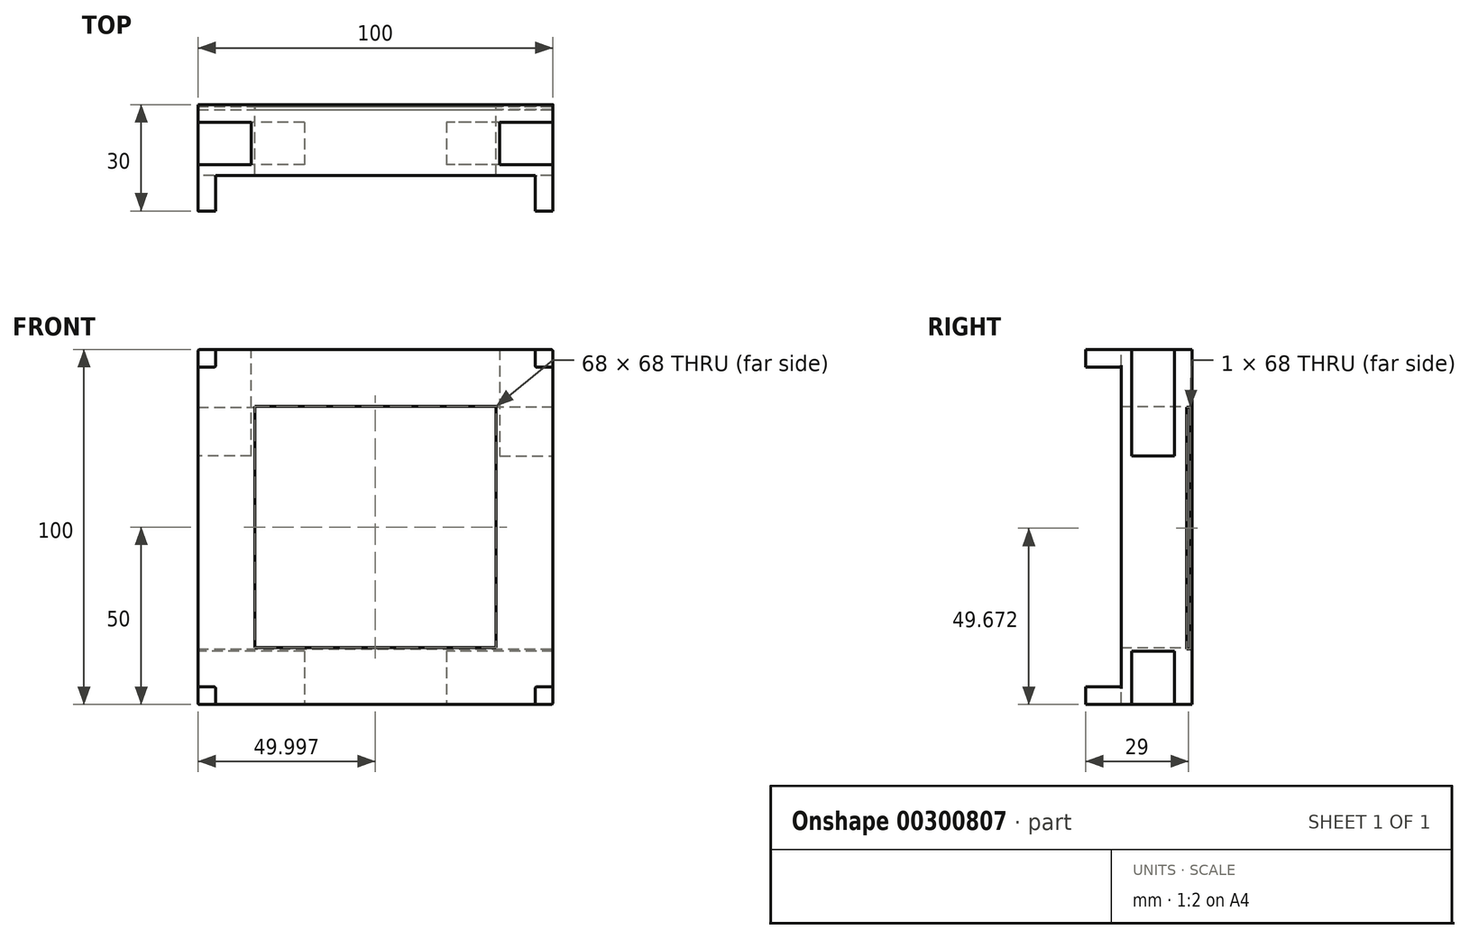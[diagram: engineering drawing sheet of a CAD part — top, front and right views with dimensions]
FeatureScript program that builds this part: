
annotation { "Feature Type Name" : "Feature", "Feature Type Description" : "" }
export const myFeature = defineFeature(function(context is Context, id is Id, definition is map)
    precondition{}
    {
        {
            var Q0;
            Q0=qCreatedBy(makeId("Front.planeOp"),FACE);
            var sketch = newSketch(context, id + "F0", { "sketchPlane" : qUnion([Q0])});
            skLineSegment(sketch, "E0.bottom", {"start": v(-49.23, 948.9) * mm, "end": v(950.77, 948.9) * mm});
            skLineSegment(sketch, "E0.top", {"start": v(-49.23, -51.1) * mm, "end": v(950.77, -51.1) * mm});
            skLineSegment(sketch, "E0.left", {"start": v(-49.23, 948.9) * mm, "end": v(-49.23, -51.1) * mm});
            skLineSegment(sketch, "E0.right", {"start": v(950.77, 948.9) * mm, "end": v(950.77, -51.1) * mm});
            skSolve(sketch);
        }
        {
            var Q0;
            Q0=qSketchRegion(id+"F0",true);
            extrude(context, id + "F1", {"entities" : qUnion([Q0]), "depth" : 300 * mm});
        }
        {
            var Q0;
            Q0=makeQuery(id+"F1.opExtrude","SWEPT_FACE",FACE,{"disambiguationData":[OSD([sQuery(id+"F0.wireOp",EDGE,"E0.bottom")])]});
            var sketch = newSketch(context, id + "F2", { "sketchPlane" : qUnion([Q0])});
            skLineSegment(sketch, "E1.bottom", {"start": v(0.77, -300) * mm, "end": v(900.77, -300) * mm});
            skLineSegment(sketch, "E1.top", {"start": v(0.77, -200) * mm, "end": v(900.77, -200) * mm});
            skLineSegment(sketch, "E1.left", {"start": v(0.77, -300) * mm, "end": v(0.77, -200) * mm});
            skLineSegment(sketch, "E1.right", {"start": v(900.77, -300) * mm, "end": v(900.77, -200) * mm});
            skSolve(sketch);
        }
        {
            var Q0;
            Q0=qSketchRegion(id+"F2",true);
            extrude(context, id + "F3", {"entities" : qUnion([Q0]), "operationType" : NewBodyOperationType.REMOVE, "endBound" : BoundingType.THROUGH_ALL, "oppositeDirection" : true, "depth" : 100 * mm});
        }
        {
            var Q0;
            Q0=makeQuery(id+"F1.opExtrude","SWEPT_FACE",FACE,{"disambiguationData":[OSD([sQuery(id+"F0.wireOp",EDGE,"E0.left")])]});
            var sketch = newSketch(context, id + "F4", { "sketchPlane" : qUnion([Q0])});
            skLineSegment(sketch, "E2.bottom", {"start": v(300, -1.1) * mm, "end": v(200, -1.1) * mm});
            skLineSegment(sketch, "E2.top", {"start": v(300, 898.9) * mm, "end": v(200, 898.9) * mm});
            skLineSegment(sketch, "E2.left", {"start": v(300, -1.1) * mm, "end": v(300, 898.9) * mm});
            skLineSegment(sketch, "E2.right", {"start": v(200, -1.1) * mm, "end": v(200, 898.9) * mm});
            skSolve(sketch);
        }
        {
            var Q0;
            Q0=qSketchRegion(id+"F4",true);
            extrude(context, id + "F5", {"entities" : qUnion([Q0]), "operationType" : NewBodyOperationType.REMOVE, "endBound" : BoundingType.THROUGH_ALL, "oppositeDirection" : true, "depth" : 25 * mm});
        }
        {
            var Q0;
            Q0=makeQuery(id+"F1.opExtrude","SWEPT_FACE",FACE,{"disambiguationData":[OSD([sQuery(id+"F0.wireOp",EDGE,"E0.top")])]});
            var sketch = newSketch(context, id + "F6", { "sketchPlane" : qUnion([Q0])});
            skLineSegment(sketch, "E3.bottom", {"start": v(250.77, 50) * mm, "end": v(-49.23, 50) * mm});
            skLineSegment(sketch, "E3.top", {"start": v(250.77, 170) * mm, "end": v(-49.23, 170) * mm});
            skLineSegment(sketch, "E3.left", {"start": v(250.77, 50) * mm, "end": v(250.77, 170) * mm});
            skLineSegment(sketch, "E3.right", {"start": v(-49.23, 50) * mm, "end": v(-49.23, 170) * mm});
            skSolve(sketch);
        }
        {
            var Q0;
            Q0=qSketchRegion(id+"F6",true);
            extrude(context, id + "F7", {"entities" : qUnion([Q0]), "operationType" : NewBodyOperationType.REMOVE, "oppositeDirection" : true, "depth" : 150 * mm});
        }
        {
            var Q0;
            Q0=makeQuery(id+"F1.opExtrude","SWEPT_FACE",FACE,{"disambiguationData":[OSD([sQuery(id+"F0.wireOp",EDGE,"E0.top")])]});
            var sketch = newSketch(context, id + "F8", { "sketchPlane" : qUnion([Q0])});
            skLineSegment(sketch, "E4.bottom", {"start": v(950.77, 50) * mm, "end": v(650.77, 50) * mm});
            skLineSegment(sketch, "E4.top", {"start": v(950.77, 170) * mm, "end": v(650.77, 170) * mm});
            skLineSegment(sketch, "E4.left", {"start": v(950.77, 50) * mm, "end": v(950.77, 170) * mm});
            skLineSegment(sketch, "E4.right", {"start": v(650.77, 50) * mm, "end": v(650.77, 170) * mm});
            skSolve(sketch);
        }
        {
            var Q0;
            Q0=qSketchRegion(id+"F8",true);
            extrude(context, id + "F9", {"entities" : qUnion([Q0]), "operationType" : NewBodyOperationType.REMOVE, "oppositeDirection" : true, "depth" : 150 * mm});
        }
        {
            var Q0;
            Q0=makeQuery(id+"F1.opExtrude","SWEPT_FACE",FACE,{"disambiguationData":[OSD([sQuery(id+"F0.wireOp",EDGE,"E0.right")])]});
            var sketch = newSketch(context, id + "F10", { "sketchPlane" : qUnion([Q0])});
            skLineSegment(sketch, "E5.bottom", {"start": v(-50, 948.9) * mm, "end": v(-170, 948.9) * mm});
            skLineSegment(sketch, "E5.top", {"start": v(-50, 648.9) * mm, "end": v(-170, 648.9) * mm});
            skLineSegment(sketch, "E5.left", {"start": v(-50, 948.9) * mm, "end": v(-50, 648.9) * mm});
            skLineSegment(sketch, "E5.right", {"start": v(-170, 948.9) * mm, "end": v(-170, 648.9) * mm});
            skSolve(sketch);
        }
        {
            var Q0;
            Q0=qSketchRegion(id+"F10",true);
            extrude(context, id + "F11", {"entities" : qUnion([Q0]), "operationType" : NewBodyOperationType.REMOVE, "oppositeDirection" : true, "depth" : 150 * mm});
        }
        {
            var Q0;
            Q0=makeQuery(id+"F1.opExtrude","SWEPT_FACE",FACE,{"disambiguationData":[OSD([sQuery(id+"F0.wireOp",EDGE,"E0.left")])]});
            var sketch = newSketch(context, id + "F12", { "sketchPlane" : qUnion([Q0])});
            skLineSegment(sketch, "E6.bottom", {"start": v(50, 648.9) * mm, "end": v(170, 648.9) * mm});
            skLineSegment(sketch, "E6.top", {"start": v(50, 948.9) * mm, "end": v(170, 948.9) * mm});
            skLineSegment(sketch, "E6.left", {"start": v(50, 648.9) * mm, "end": v(50, 948.9) * mm});
            skLineSegment(sketch, "E6.right", {"start": v(170, 648.9) * mm, "end": v(170, 948.9) * mm});
            skSolve(sketch);
        }
        {
            var Q0;
            Q0=qSketchRegion(id+"F12",true);
            extrude(context, id + "F13", {"entities" : qUnion([Q0]), "operationType" : NewBodyOperationType.REMOVE, "oppositeDirection" : true, "depth" : 150 * mm});
        }
        {
            var Q0;
            {var subQ0=sQuery(id+"F0.wireOp",EDGE,"E0.right");var subQ1=sQuery(id+"F0.wireOp",EDGE,"E0.top");Q0=makeQuery(id+"F9.boolean.opBoolean","SPLIT",EDGE,{"disambiguationData":[TD([makeQuery(id+"F9.opExtrude","SWEPT_FACE",FACE,{"disambiguationData":[OSD([sQuery(id+"F8.wireOp",EDGE,"E4.top")])]})])],"derivedFrom":makeQuery(id+"F1.opExtrude","SWEPT_EDGE",EDGE,{"disambiguationData":[OSD([subQ1,subQ0])]})});}
            var Q1;
            Q1=makeQuery(id+"F3.boolean.opBoolean","INTERSECT",EDGE,{"derivedFrom":[makeQuery(id+"F1.opExtrude","SWEPT_FACE",FACE,{"disambiguationData":[OSD([sQuery(id+"F0.wireOp",EDGE,"E0.top")])]}),makeQuery(id+"F3.opExtrude","SWEPT_FACE",FACE,{"disambiguationData":[OSD([sQuery(id+"F2.wireOp",EDGE,"E1.right")])]})]});
            var Q2;
            Q2=makeQuery(id+"F5.boolean.opBoolean","INTERSECT",EDGE,{"derivedFrom":[makeQuery(id+"F1.opExtrude","SWEPT_FACE",FACE,{"disambiguationData":[OSD([sQuery(id+"F0.wireOp",EDGE,"E0.right")])]}),makeQuery(id+"F5.opExtrude","SWEPT_FACE",FACE,{"disambiguationData":[OSD([sQuery(id+"F4.wireOp",EDGE,"E2.bottom")])]})]});
            var Q3;
            Q3=makeQuery(id+"F5.boolean.opBoolean","INTERSECT",EDGE,{"derivedFrom":[makeQuery(id+"F3.boolean.opBoolean","COPY",FACE,{"derivedFrom":makeQuery(id+"F3.opExtrude","SWEPT_FACE",FACE,{"disambiguationData":[OSD([sQuery(id+"F2.wireOp",EDGE,"E1.right")])]})}),makeQuery(id+"F5.opExtrude","SWEPT_FACE",FACE,{"disambiguationData":[OSD([sQuery(id+"F4.wireOp",EDGE,"E2.bottom")])]})]});
            var Q4;
            {var subQ0=sQuery(id+"F0.wireOp",EDGE,"E0.left");var subQ1=sQuery(id+"F0.wireOp",EDGE,"E0.top");Q4=makeQuery(id+"F7.boolean.opBoolean","SPLIT",EDGE,{"disambiguationData":[TD([makeQuery(id+"F7.opExtrude","SWEPT_FACE",FACE,{"disambiguationData":[OSD([sQuery(id+"F6.wireOp",EDGE,"E3.top")])]})])],"derivedFrom":makeQuery(id+"F1.opExtrude","SWEPT_EDGE",EDGE,{"disambiguationData":[OSD([subQ1,subQ0])]})});}
            var Q5;
            Q5=makeQuery(id+"F3.boolean.opBoolean","INTERSECT",EDGE,{"derivedFrom":[makeQuery(id+"F1.opExtrude","SWEPT_FACE",FACE,{"disambiguationData":[OSD([sQuery(id+"F0.wireOp",EDGE,"E0.top")])]}),makeQuery(id+"F3.opExtrude","SWEPT_FACE",FACE,{"disambiguationData":[OSD([sQuery(id+"F2.wireOp",EDGE,"E1.left")])]})]});
            var Q6;
            Q6=makeQuery(id+"F5.boolean.opBoolean","COPY",EDGE,{"derivedFrom":makeQuery(id+"F5.opExtrude","CAP_EDGE",EDGE,{"disambiguationData":[OSD([sQuery(id+"F4.wireOp",EDGE,"E2.bottom")])],"isStart":true})});
            var Q7;
            Q7=makeQuery(id+"F5.boolean.opBoolean","INTERSECT",EDGE,{"derivedFrom":[makeQuery(id+"F3.boolean.opBoolean","COPY",FACE,{"derivedFrom":makeQuery(id+"F3.opExtrude","SWEPT_FACE",FACE,{"disambiguationData":[OSD([sQuery(id+"F2.wireOp",EDGE,"E1.left")])]})}),makeQuery(id+"F5.opExtrude","SWEPT_FACE",FACE,{"disambiguationData":[OSD([sQuery(id+"F4.wireOp",EDGE,"E2.bottom")])]})]});
            var Q8;
            {var subQ0=sQuery(id+"F0.wireOp",EDGE,"E0.bottom");var subQ1=sQuery(id+"F0.wireOp",EDGE,"E0.left");Q8=makeQuery(id+"F13.boolean.opBoolean","SPLIT",EDGE,{"disambiguationData":[TD([makeQuery(id+"F13.opExtrude","SWEPT_FACE",FACE,{"disambiguationData":[OSD([sQuery(id+"F12.wireOp",EDGE,"E6.right")])]})])],"derivedFrom":makeQuery(id+"F1.opExtrude","SWEPT_EDGE",EDGE,{"disambiguationData":[OSD([subQ0,subQ1])]})});}
            var Q9;
            Q9=makeQuery(id+"F3.boolean.opBoolean","COPY",EDGE,{"derivedFrom":makeQuery(id+"F3.opExtrude","CAP_EDGE",EDGE,{"disambiguationData":[OSD([sQuery(id+"F2.wireOp",EDGE,"E1.left")])],"isStart":true})});
            var Q10;
            Q10=makeQuery(id+"F5.boolean.opBoolean","COPY",EDGE,{"derivedFrom":makeQuery(id+"F5.opExtrude","CAP_EDGE",EDGE,{"disambiguationData":[OSD([sQuery(id+"F4.wireOp",EDGE,"E2.top")])],"isStart":true})});
            var Q11;
            Q11=makeQuery(id+"F5.boolean.opBoolean","INTERSECT",EDGE,{"derivedFrom":[makeQuery(id+"F3.boolean.opBoolean","COPY",FACE,{"derivedFrom":makeQuery(id+"F3.opExtrude","SWEPT_FACE",FACE,{"disambiguationData":[OSD([sQuery(id+"F2.wireOp",EDGE,"E1.left")])]})}),makeQuery(id+"F5.opExtrude","SWEPT_FACE",FACE,{"disambiguationData":[OSD([sQuery(id+"F4.wireOp",EDGE,"E2.top")])]})]});
            var Q12;
            {var subQ0=sQuery(id+"F0.wireOp",EDGE,"E0.bottom");var subQ1=sQuery(id+"F0.wireOp",EDGE,"E0.right");Q12=makeQuery(id+"F11.boolean.opBoolean","SPLIT",EDGE,{"disambiguationData":[TD([makeQuery(id+"F11.opExtrude","SWEPT_FACE",FACE,{"disambiguationData":[OSD([sQuery(id+"F10.wireOp",EDGE,"E5.right")])]})])],"derivedFrom":makeQuery(id+"F1.opExtrude","SWEPT_EDGE",EDGE,{"disambiguationData":[OSD([subQ0,subQ1])]})});}
            var Q13;
            Q13=makeQuery(id+"F5.boolean.opBoolean","INTERSECT",EDGE,{"derivedFrom":[makeQuery(id+"F1.opExtrude","SWEPT_FACE",FACE,{"disambiguationData":[OSD([sQuery(id+"F0.wireOp",EDGE,"E0.right")])]}),makeQuery(id+"F5.opExtrude","SWEPT_FACE",FACE,{"disambiguationData":[OSD([sQuery(id+"F4.wireOp",EDGE,"E2.top")])]})]});
            var Q14;
            Q14=makeQuery(id+"F5.boolean.opBoolean","INTERSECT",EDGE,{"derivedFrom":[makeQuery(id+"F3.boolean.opBoolean","COPY",FACE,{"derivedFrom":makeQuery(id+"F3.opExtrude","SWEPT_FACE",FACE,{"disambiguationData":[OSD([sQuery(id+"F2.wireOp",EDGE,"E1.right")])]})}),makeQuery(id+"F5.opExtrude","SWEPT_FACE",FACE,{"disambiguationData":[OSD([sQuery(id+"F4.wireOp",EDGE,"E2.top")])]})]});
            var Q15;
            Q15=makeQuery(id+"F3.boolean.opBoolean","COPY",EDGE,{"derivedFrom":makeQuery(id+"F3.opExtrude","CAP_EDGE",EDGE,{"disambiguationData":[OSD([sQuery(id+"F2.wireOp",EDGE,"E1.right")])],"isStart":true})});
            fillet(context, id + "F14", {"entities" : qUnion([Q0, Q1, Q2, Q3, Q4, Q5, Q6, Q7, Q8, Q9, Q10, Q11, Q12, Q13, Q14, Q15]), "radius" : 5 * mm, "tangentPropagation" : true, "allowEdgeOverflow" : false});
        }
        {
            var Q0;
            {var subQ0=sQuery(id+"F0.wireOp",EDGE,"E0.bottom");var subQ1=sQuery(id+"F0.wireOp",EDGE,"E0.right");Q0=makeQuery(id+"F11.boolean.opBoolean","SPLIT",EDGE,{"disambiguationData":[TD([makeQuery(id+"F11.opExtrude","SWEPT_FACE",FACE,{"disambiguationData":[OSD([sQuery(id+"F10.wireOp",EDGE,"E5.left")])]})])],"derivedFrom":makeQuery(id+"F1.opExtrude","SWEPT_EDGE",EDGE,{"disambiguationData":[OSD([subQ0,subQ1])]})});}
            var Q1;
            {var subQ0=sQuery(id+"F0.wireOp",EDGE,"E0.right");var subQ1=sQuery(id+"F0.wireOp",EDGE,"E0.top");Q1=makeQuery(id+"F9.boolean.opBoolean","SPLIT",EDGE,{"disambiguationData":[TD([makeQuery(id+"F9.opExtrude","SWEPT_FACE",FACE,{"disambiguationData":[OSD([sQuery(id+"F8.wireOp",EDGE,"E4.bottom")])]})])],"derivedFrom":makeQuery(id+"F1.opExtrude","SWEPT_EDGE",EDGE,{"disambiguationData":[OSD([subQ1,subQ0])]})});}
            var Q2;
            {var subQ0=sQuery(id+"F0.wireOp",EDGE,"E0.left");var subQ1=sQuery(id+"F0.wireOp",EDGE,"E0.top");Q2=makeQuery(id+"F7.boolean.opBoolean","SPLIT",EDGE,{"disambiguationData":[TD([makeQuery(id+"F7.opExtrude","SWEPT_FACE",FACE,{"disambiguationData":[OSD([sQuery(id+"F6.wireOp",EDGE,"E3.bottom")])]})])],"derivedFrom":makeQuery(id+"F1.opExtrude","SWEPT_EDGE",EDGE,{"disambiguationData":[OSD([subQ1,subQ0])]})});}
            var Q3;
            {var subQ0=sQuery(id+"F0.wireOp",EDGE,"E0.bottom");var subQ1=sQuery(id+"F0.wireOp",EDGE,"E0.left");Q3=makeQuery(id+"F13.boolean.opBoolean","SPLIT",EDGE,{"disambiguationData":[TD([makeQuery(id+"F13.opExtrude","SWEPT_FACE",FACE,{"disambiguationData":[OSD([sQuery(id+"F12.wireOp",EDGE,"E6.left")])]})])],"derivedFrom":makeQuery(id+"F1.opExtrude","SWEPT_EDGE",EDGE,{"disambiguationData":[OSD([subQ0,subQ1])]})});}
            fillet(context, id + "F15", {"entities" : qUnion([Q0, Q1, Q2, Q3]), "radius" : 5 * mm, "tangentPropagation" : true, "allowEdgeOverflow" : false});
        }
        {
            var Q0;
            Q0=makeQuery(id+"F1.opExtrude","CAP_FACE",FACE,{"disambiguationData":[OSD([sQuery(id+"F0.wireOp",EDGE,"E0.bottom"),sQuery(id+"F0.wireOp",EDGE,"E0.top"),sQuery(id+"F0.wireOp",EDGE,"E0.left"),sQuery(id+"F0.wireOp",EDGE,"E0.right")])],"isStart":true});
            var sketch = newSketch(context, id + "F16", { "sketchPlane" : qUnion([Q0])});
            skLineSegment(sketch, "E7.bottom", {"start": v(-790.77, 788.9) * mm, "end": v(-110.77, 788.9) * mm});
            skLineSegment(sketch, "E7.top", {"start": v(-790.77, 108.9) * mm, "end": v(-110.77, 108.9) * mm});
            skLineSegment(sketch, "E7.left", {"start": v(-790.77, 788.9) * mm, "end": v(-790.77, 108.9) * mm});
            skLineSegment(sketch, "E7.right", {"start": v(-110.77, 788.9) * mm, "end": v(-110.77, 108.9) * mm});
            skSolve(sketch);
        }
        {
            var Q0;
            Q0=qSketchRegion(id+"F16",true);
            extrude(context, id + "F17", {"entities" : qUnion([Q0]), "operationType" : NewBodyOperationType.REMOVE, "endBound" : BoundingType.THROUGH_ALL, "oppositeDirection" : true, "depth" : 25 * mm});
        }
        {
            var Q0;
            Q0=makeQuery(id+"F17.boolean.opBoolean","COPY",FACE,{"derivedFrom":makeQuery(id+"F17.opExtrude","SWEPT_FACE",FACE,{"disambiguationData":[OSD([sQuery(id+"F16.wireOp",EDGE,"E7.right")])]})});
            var sketch = newSketch(context, id + "F18", { "sketchPlane" : qUnion([Q0])});
            skLineSegment(sketch, "E8.bottom", {"start": v(-5, 785.62) * mm, "end": v(-15, 785.62) * mm});
            skLineSegment(sketch, "E8.top", {"start": v(-5, 105.62) * mm, "end": v(-15, 105.62) * mm});
            skLineSegment(sketch, "E8.left", {"start": v(-5, 785.62) * mm, "end": v(-5, 105.62) * mm});
            skLineSegment(sketch, "E8.right", {"start": v(-15, 785.62) * mm, "end": v(-15, 105.62) * mm});
            skSolve(sketch);
        }
        {
            var Q0;
            Q0=qSketchRegion(id+"F18",true);
            extrude(context, id + "F19", {"entities" : qUnion([Q0]), "operationType" : NewBodyOperationType.REMOVE, "endBound" : BoundingType.THROUGH_ALL, "oppositeDirection" : true, "depth" : 25 * mm});
        }
        {
            var Q0;
            Q0=qSketchRegion(id+"F18",true);
            extrude(context, id + "F20", {"entities" : qUnion([Q0]), "operationType" : NewBodyOperationType.REMOVE, "endBound" : BoundingType.THROUGH_ALL, "depth" : 25 * mm});
        }
        {
            var Q0;
            Q0=makeQuery(id+"F1.opExtrude","SWEPT_BODY",BODY,{"disambiguationData":[OSD([sQuery(id+"F0.wireOp",EDGE,"E0.bottom"),sQuery(id+"F0.wireOp",EDGE,"E0.top"),sQuery(id+"F0.wireOp",EDGE,"E0.left"),sQuery(id+"F0.wireOp",EDGE,"E0.right")])]});
            var Q1;
            Q1=qCreatedBy(makeId("Origin.pointOp"),VERTEX);
            var Q2;
            Q2=qCreatedBy(makeId("Origin.pointOp"),VERTEX);
            transform(context, id + "F21", {"entities" : qUnion([Q0]), "transformType" : TransformType.SCALE_UNIFORMLY, "scale" : 0.1, "scalePoint" : qUnion([Q2]), "makeCopy" : false});
        }
    });
